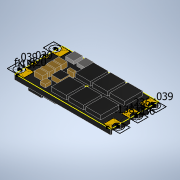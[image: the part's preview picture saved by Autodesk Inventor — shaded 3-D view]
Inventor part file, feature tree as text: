
AUTODESK INVENTOR PART (.ipt)
format: ipt  version: 2022 (Build 260153000, 153)  size: 470,528 bytes
history: native  units: in
note: dims shown in document units (in); Inventor stores cm internally (conversion verified against a paired STEP export)
features: extrude x12, sketch x11, mirror x1
ambient origin geometry x8: Origin, YZ Plane, XZ Plane, XY Plane, X Axis, Y Axis, Z Axis, Center Point
bodies: Solid1 (feature_tree)
feature tree (24):
  extrude  "Extrusion1"  Depth=0.6299in
  sketch  "Sketch2"  dims[d2=0.0344in d3=0.0in d4=0.0394in]
  extrude  "Extrusion2"  Depth=0.0394in
  extrude  "Extrusion3"  Depth=0.7874in
  mirror  "Mirror1"
  extrude  "Extrusion4"  Depth=0.1378in
  extrude  "Extrusion5"  Depth=0.0394in
  extrude  "Extrusion6"  Depth=0.0689in TaperAngle=0.0deg
  extrude  "Extrusion7"  Depth=0.0197in
  extrude  "Extrusion8"  Depth=0.1969in
  extrude  "Extrusion9"  Depth=0.1673in
  extrude  "Extrusion10"  Depth=0.2264in
  extrude  "Extrusion11"  Depth=0.1083in
  extrude  "Extrusion12"  Depth=0.1181in
  sketch  "Sketch1"  dims[d0=1.2598in d1=0.6299in]
  sketch  "Sketch3"  dims[d5=0.1181in d6=0.7874in d8=0.2362in d9=0.3937in d11=1.0in]
  sketch  "Sketch4"  dims[d13=0.2165in d14=0.1378in]
  sketch  "Sketch5"  dims[d15=0.7874in d17=0.2362in d18=0.3937in d20=1.0in d22=0.0394in]
  sketch  "Sketch6"  dims[d23=0.1575in d24=0.0689in d25=0.0in]
  sketch  "Sketch7"  dims[d26=0.0004in d27=0.0in d28=0.0197in]
  sketch  "Sketch8"  dims[d29=0.0197in d30=0.1969in]
  sketch  "Sketch9"  dims[d31=0.2362in d32=0.1673in]
  sketch  "Sketch10"  dims[d33=0.0394in d34=1.1811in d36=0.2264in d37=0.3937in d39=1.0in]
  sketch  "Sketch11"  dims[d41=0.0531in d42=0.0in d43=0.1083in d44=0.1181in d45=0.0197in d46=0.1772in d47=0.7874in d49=0.1476in d50=0.3937in d52=1.0in d54=0.0394in d55=0.0in d56=0.1122in d57=0.0689in d58=1.5748in d60=0.0846in d61=0.3937in d63=1.0in d65=0.0984in d66=0.1575in d67=0.1181in d68=0.1181in d69=0.1713in d70=0.315in d71=0.0787in d72=0.0394in d73=0.3543in d74=0.3346in d75=0.0591in d76=0.0in d77=0.0689in d78=0.0787in d79=0.0394in d80=0.2953in d81=0.0394in d82=0.0in d83=0.1772in d84=0.1181in d85=0.0591in d86=0.1181in d87=0.0925in d88=0.0in d89=0.1673in d90=0.0886in d91=0.0591in d92=0.315in d93=0.0689in d94=0.0in d95=0.1181in d96=0.0689in d97=0.1831in d98=0.1476in d99=1.1811in d101=0.0846in d102=0.3937in d104=1.0in d106=0.0689in d107=0.0in d108=0.128in d109=0.0787in d110=0.128in d111=0.0787in d112=0.128in d113=0.0787in d114=0.0197in d115=0.0138in d116=0.3543in d117=0.2953in d118=0.315in d119=0.0591in d120=0.0in d121=0.1969in d122=0.1969in d123=0.1575in d124=0.1575in d125=0.5118in d126=0.1969in d127=0.2854in d128=0.1772in d129=0.0394in d130=0.0in]
